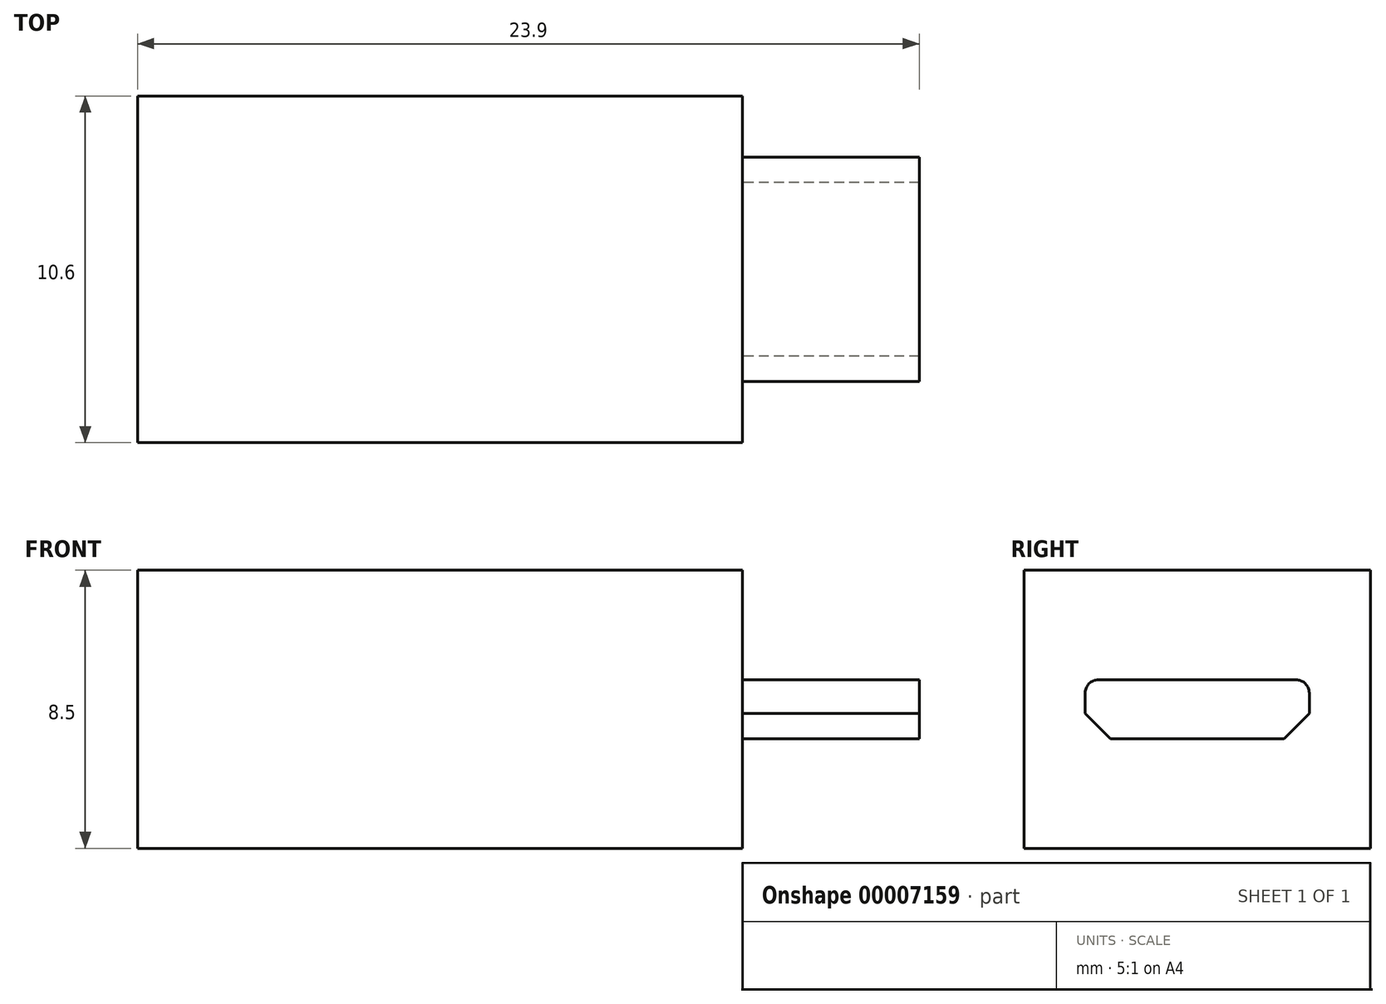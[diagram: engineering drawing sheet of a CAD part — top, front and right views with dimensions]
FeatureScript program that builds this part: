
annotation { "Feature Type Name" : "Feature", "Feature Type Description" : "" }
export const myFeature = defineFeature(function(context is Context, id is Id, definition is map)
    precondition{}
    {
        {
            var Q0;
            Q0=qCreatedBy(makeId("Top.planeOp"),FACE);
            var sketch = newSketch(context, id + "F0", { "sketchPlane" : qUnion([Q0])});
            skLineSegment(sketch, "E0.bottom", {"start": v(0, 0) * mm, "end": v(18.5, 0) * mm});
            skLineSegment(sketch, "E0.top", {"start": v(0, 10.6) * mm, "end": v(18.5, 10.6) * mm});
            skLineSegment(sketch, "E0.left", {"start": v(0, 0) * mm, "end": v(0, 10.6) * mm});
            skLineSegment(sketch, "E0.right", {"start": v(18.5, 0) * mm, "end": v(18.5, 10.6) * mm});
            skSolve(sketch);
        }
        {
            var Q0;
            Q0 = qSketchRegion(id + "F0", true);
            extrude(context, id + "F1", {"entities" : qUnion([Q0]), "depth" : 8.5 * mm});
        }
        {
            var Q0;
            Q0=makeQuery(id+"F1.opExtrude","SWEPT_FACE",FACE,{"disambiguationData":[OSD([sQuery(id+"F0.wireOp",EDGE,"E0.right")])]});
            var sketch = newSketch(context, id + "F2", { "sketchPlane" : qUnion([Q0])});
            skLineSegment(sketch, "E1", {"start": v(2.27, 5.15) * mm, "end": v(8.32, 5.15) * mm});
            skLineSegment(sketch, "E2", {"start": v(8.72, 4.75) * mm, "end": v(8.72, 4.12) * mm});
            skLineSegment(sketch, "E3", {"start": v(8.72, 4.12) * mm, "end": v(7.95, 3.35) * mm});
            skLineSegment(sketch, "E4", {"start": v(7.95, 3.35) * mm, "end": v(2.65, 3.35) * mm});
            skLineSegment(sketch, "E5", {"start": v(2.65, 3.35) * mm, "end": v(1.87, 4.12) * mm});
            skLineSegment(sketch, "E6", {"start": v(1.87, 4.12) * mm, "end": v(1.87, 4.75) * mm});
            skPoint(sketch, "E7.visualSharp", {"position": v(1.87, 5.15) * mm});
            skArc(sketch, "E7.filletArc", {"start": v(2.27, 5.15) * mm, "mid": v(2, 5.03) * mm, "end": v(1.87, 4.75) * mm});
            skPoint(sketch, "E8.visualSharp", {"position": v(8.72, 5.15) * mm});
            skArc(sketch, "E8.filletArc", {"start": v(8.72, 4.75) * mm, "mid": v(8.6, 5.03) * mm, "end": v(8.32, 5.15) * mm});
            skSolve(sketch);
        }
        {
            var Q0;
            Q0=makeQuery(id+"F2.imprint","IMPRINT",FACE,{"disambiguationData":[TD([[makeQuery(id+"F2.imprint","IMPRINT",EDGE,{"derivedFrom":sQuery(id+"F2.wireOp",EDGE,"E1")}),-1.0]])]});
            extrude(context, id + "F3", {"entities" : qUnion([Q0]), "operationType" : NewBodyOperationType.ADD, "depth" : 5.4 * mm});
        }
    });
